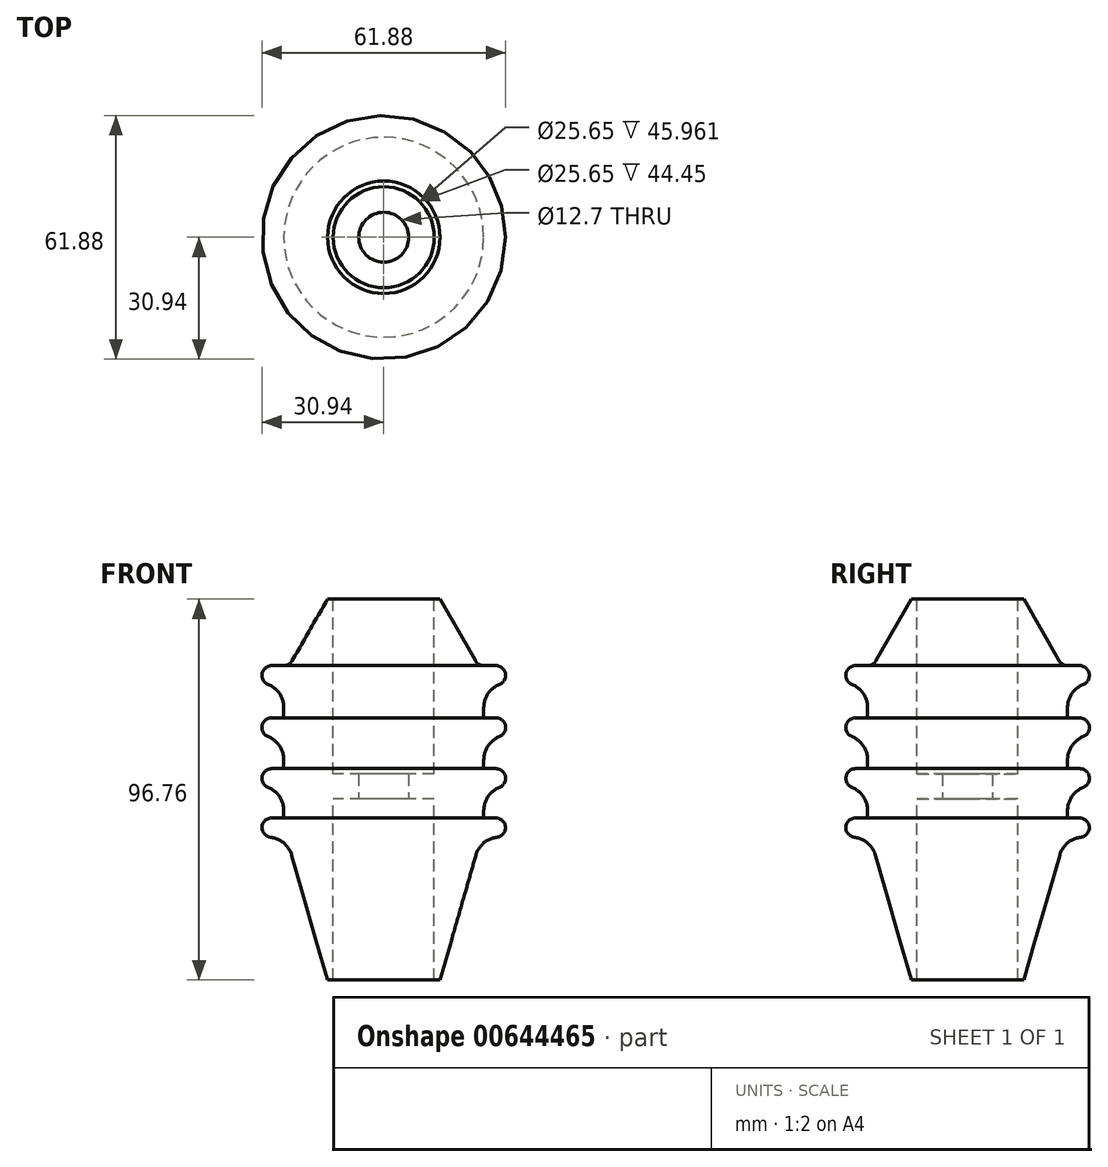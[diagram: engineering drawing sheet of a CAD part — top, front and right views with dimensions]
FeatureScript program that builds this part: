
annotation { "Feature Type Name" : "Feature", "Feature Type Description" : "" }
export const myFeature = defineFeature(function(context is Context, id is Id, definition is map)
    precondition{}
    {
        {
            var Q0;
            Q0=qCreatedBy(makeId("Front.planeOp"),FACE);
            var sketch = newSketch(context, id + "F0", { "sketchPlane" : qUnion([Q0])});
            skLineSegment(sketch, "E0", {"start": v(0, 0) * mm, "end": v(0, 96.76) * mm});
            skLineSegment(sketch, "E1", {"start": v(0, 96.76) * mm, "end": v(0, 58.06) * mm});
            skLineSegment(sketch, "E2", {"start": v(0, 0) * mm, "end": v(0, 38.7) * mm});
            skLineSegment(sketch, "E3", {"start": v(0, 96.76) * mm, "end": v(-14.29, 96.76) * mm});
            skLineSegment(sketch, "E4", {"start": v(-14.29, 96.76) * mm, "end": v(-14.29, 0) * mm});
            skLineSegment(sketch, "E5", {"start": v(-14.29, 0) * mm, "end": v(0, 0) * mm});
            skLineSegment(sketch, "E6", {"start": v(0, 96.76) * mm, "end": v(0, 77.4) * mm});
            skLineSegment(sketch, "E7", {"start": v(-25.4, 77.4) * mm, "end": v(-25.4, 38.7) * mm});
            skLineSegment(sketch, "E8", {"start": v(-25.4, 77.4) * mm, "end": v(-14.29, 96.76) * mm});
            skLineSegment(sketch, "E9", {"start": v(-25.4, 38.7) * mm, "end": v(-14.29, 0) * mm});
            skLineSegment(sketch, "E10", {"start": v(-25.4, 77.4) * mm, "end": v(-25.4, 64.14) * mm});
            skLineSegment(sketch, "E11", {"start": v(-25.4, 64.14) * mm, "end": v(-25.4, 51.24) * mm});
            skLineSegment(sketch, "E12", {"start": v(-25.4, 77.4) * mm, "end": v(-25.4, 74.95) * mm});
            skLineSegment(sketch, "E13", {"start": v(-25.4, 77.4) * mm, "end": v(-25.4, 79.87) * mm});
            skLineSegment(sketch, "E14", {"start": v(-25.4, 79.87) * mm, "end": v(0, 79.87) * mm});
            skLineSegment(sketch, "E15", {"start": v(-25.4, 64.14) * mm, "end": v(-25.4, 66.6) * mm});
            skLineSegment(sketch, "E16", {"start": v(-25.4, 64.14) * mm, "end": v(-25.4, 61.68) * mm});
            skLineSegment(sketch, "E17", {"start": v(-25.4, 61.68) * mm, "end": v(0, 61.68) * mm});
            skLineSegment(sketch, "E18", {"start": v(-25.4, 66.6) * mm, "end": v(0, 66.6) * mm});
            skLineSegment(sketch, "E19", {"start": v(-25.4, 74.95) * mm, "end": v(0, 74.95) * mm});
            skLineSegment(sketch, "E20", {"start": v(-25.4, 51.24) * mm, "end": v(-25.4, 53.7) * mm});
            skLineSegment(sketch, "E21", {"start": v(-25.4, 51.24) * mm, "end": v(-25.4, 48.77) * mm});
            skLineSegment(sketch, "E22", {"start": v(-25.4, 48.77) * mm, "end": v(0, 48.77) * mm});
            skLineSegment(sketch, "E23", {"start": v(-25.4, 53.7) * mm, "end": v(0, 53.7) * mm});
            skLineSegment(sketch, "E24", {"start": v(-25.4, 38.7) * mm, "end": v(-25.4, 41.17) * mm});
            skLineSegment(sketch, "E25", {"start": v(-25.4, 38.7) * mm, "end": v(-25.4, 36.24) * mm});
            skLineSegment(sketch, "E26", {"start": v(-25.4, 36.24) * mm, "end": v(0, 36.24) * mm});
            skLineSegment(sketch, "E27", {"start": v(-25.4, 41.17) * mm, "end": v(0, 41.17) * mm});
            skLineSegment(sketch, "E28", {"start": v(-25.4, 79.87) * mm, "end": v(-28.48, 79.87) * mm});
            skLineSegment(sketch, "E29", {"start": v(-25.4, 36.24) * mm, "end": v(-28.48, 36.24) * mm});
            skLineSegment(sketch, "E30", {"start": v(-28.48, 36.24) * mm, "end": v(-28.48, 41.17) * mm});
            skLineSegment(sketch, "E31", {"start": v(-25.4, 74.95) * mm, "end": v(-28.48, 74.95) * mm});
            skLineSegment(sketch, "E32", {"start": v(-25.4, 66.6) * mm, "end": v(-28.48, 66.6) * mm});
            skLineSegment(sketch, "E33", {"start": v(-25.4, 61.68) * mm, "end": v(-28.48, 61.68) * mm});
            skLineSegment(sketch, "E34", {"start": v(-25.4, 53.7) * mm, "end": v(-28.48, 53.7) * mm});
            skLineSegment(sketch, "E35", {"start": v(-25.4, 48.77) * mm, "end": v(-28.48, 48.77) * mm});
            skLineSegment(sketch, "E36", {"start": v(-25.4, 41.17) * mm, "end": v(-28.48, 41.17) * mm});
            skLineSegment(sketch, "E37.trimOffspring", {"start": v(-28.48, 74.95) * mm, "end": v(-28.48, 79.87) * mm});
            skLineSegment(sketch, "E38.trimOffspring", {"start": v(-28.48, 61.68) * mm, "end": v(-28.48, 66.6) * mm});
            skLineSegment(sketch, "E39.trimOffspring", {"start": v(-28.48, 48.77) * mm, "end": v(-28.48, 53.7) * mm});
            skArc(sketch, "E40", {"start": v(-28.48, 79.87) * mm, "mid": v(-30.94, 77.4) * mm, "end": v(-28.48, 74.95) * mm});
            skArc(sketch, "E41", {"start": v(-28.48, 66.6) * mm, "mid": v(-30.94, 64.14) * mm, "end": v(-28.48, 61.68) * mm});
            skArc(sketch, "E42", {"start": v(-28.48, 53.7) * mm, "mid": v(-30.94, 51.24) * mm, "end": v(-28.48, 48.77) * mm});
            skArc(sketch, "E43", {"start": v(-28.48, 41.17) * mm, "mid": v(-30.94, 38.7) * mm, "end": v(-28.48, 36.24) * mm});
            skLineSegment(sketch, "E44", {"start": v(-24.7, 36.24) * mm, "end": v(-14.29, 0) * mm});
            skLineSegment(sketch, "E45", {"start": v(-14.29, 0) * mm, "end": v(-16.02, 6.04) * mm});
            skLineSegment(sketch, "E46", {"start": v(-24.7, 36.24) * mm, "end": v(-18.26, 13.85) * mm});
            skLineSegment(sketch, "E47", {"start": v(-16.02, 6.04) * mm, "end": v(-18.26, 13.85) * mm});
            skLineSegment(sketch, "E48", {"start": v(-18.26, 13.85) * mm, "end": v(-20.5, 21.66) * mm});
            skLineSegment(sketch, "E49", {"start": v(-20.5, 21.66) * mm, "end": v(-19.76, 19.06) * mm});
            skLineSegment(sketch, "E50", {"start": v(-19.76, 19.06) * mm, "end": v(-19.01, 16.45) * mm});
            skLineSegment(sketch, "E51", {"start": v(-19.01, 16.45) * mm, "end": v(-18.26, 13.85) * mm});
            skLineSegment(sketch, "E52", {"start": v(-18.26, 13.85) * mm, "end": v(-17.52, 11.24) * mm});
            skLineSegment(sketch, "E53", {"start": v(-17.52, 11.24) * mm, "end": v(-16.77, 8.64) * mm});
            skLineSegment(sketch, "E54", {"start": v(-16.77, 8.64) * mm, "end": v(-16.02, 6.04) * mm});
            skLineSegment(sketch, "E55", {"start": v(-20.5, 21.66) * mm, "end": v(-23.05, 21.66) * mm});
            skLineSegment(sketch, "E56", {"start": v(-23.05, 21.66) * mm, "end": v(-23.05, 9.97) * mm});
            skLineSegment(sketch, "E57", {"start": v(-17.52, 11.24) * mm, "end": v(-23.05, 11.24) * mm});
            skLineSegment(sketch, "E58", {"start": v(-23.05, 11.24) * mm, "end": v(-17.52, 11.24) * mm});
            skLineSegment(sketch, "E59", {"start": v(-18.26, 13.85) * mm, "end": v(-23.05, 13.85) * mm});
            skLineSegment(sketch, "E60", {"start": v(-23.05, 13.85) * mm, "end": v(-18.26, 13.85) * mm});
            skLineSegment(sketch, "E61", {"start": v(-19.01, 16.45) * mm, "end": v(-23.05, 16.45) * mm});
            skLineSegment(sketch, "E62", {"start": v(-23.05, 16.45) * mm, "end": v(-19.01, 16.45) * mm});
            skLineSegment(sketch, "E63", {"start": v(-19.76, 19.06) * mm, "end": v(-23.05, 19.06) * mm});
            skLineSegment(sketch, "E64", {"start": v(-23.05, 19.06) * mm, "end": v(-19.76, 19.06) * mm});
            skArc(sketch, "E65", {"start": v(-23.05, 22.93) * mm, "mid": v(-24.32, 21.66) * mm, "end": v(-23.05, 20.39) * mm});
            skArc(sketch, "E66", {"start": v(-23.05, 20.33) * mm, "mid": v(-24.32, 19.06) * mm, "end": v(-23.05, 17.79) * mm});
            skArc(sketch, "E67", {"start": v(-23.05, 17.72) * mm, "mid": v(-24.32, 16.45) * mm, "end": v(-23.05, 15.18) * mm});
            skArc(sketch, "E68", {"start": v(-23.05, 15.12) * mm, "mid": v(-24.32, 13.85) * mm, "end": v(-23.05, 12.58) * mm});
            skArc(sketch, "E69", {"start": v(-23.05, 12.51) * mm, "mid": v(-24.32, 11.24) * mm, "end": v(-23.05, 9.97) * mm});
            skLineSegment(sketch, "E70", {"start": v(-23.05, 22.93) * mm, "end": v(-20.87, 22.93) * mm});
            skLineSegment(sketch, "E71", {"start": v(-23.05, 9.97) * mm, "end": v(-17.15, 9.97) * mm});
            skPoint(sketch, "E72.end.orphan", {"position": v(-23.05, 8.64) * mm});
            skPoint(sketch, "E73.start.orphan", {"position": v(-23.05, 6.04) * mm});
            skSolve(sketch);
        }
        {
            var Q0;
            Q0=qSketchRegion(id+"F0",true);
            var Q1;
            Q1=sQuery(id+"F0.wireOp",EDGE,"E6");
            revolve(context, id + "F1", {"entities" : qUnion([Q0]), "axis" : qUnion([Q1]), "revolveType" : RevolveType.FULL});
        }
        {
            var Q0;
            Q0=makeQuery(id+"F1.opRevolve","SWEPT_EDGE",EDGE,{"disambiguationData":[OSD([sQuery(id+"F0.wireOp",EDGE,"E9"),sQuery(id+"F0.wireOp",EDGE,"E26")])]});
            var Q1;
            Q1=makeQuery(id+"F1.opRevolve","SWEPT_EDGE",EDGE,{"disambiguationData":[OSD([sQuery(id+"F0.wireOp",EDGE,"E7"),sQuery(id+"F0.wireOp",EDGE,"E21"),sQuery(id+"F0.wireOp",EDGE,"E22"),sQuery(id+"F0.wireOp",EDGE,"E35")])]});
            var Q2;
            Q2=makeQuery(id+"F1.opRevolve","SWEPT_EDGE",EDGE,{"disambiguationData":[OSD([sQuery(id+"F0.wireOp",EDGE,"E11"),sQuery(id+"F0.wireOp",EDGE,"E16"),sQuery(id+"F0.wireOp",EDGE,"E17"),sQuery(id+"F0.wireOp",EDGE,"E33")])]});
            var Q3;
            Q3=makeQuery(id+"F1.opRevolve","SWEPT_EDGE",EDGE,{"disambiguationData":[OSD([sQuery(id+"F0.wireOp",EDGE,"E10"),sQuery(id+"F0.wireOp",EDGE,"E12"),sQuery(id+"F0.wireOp",EDGE,"E19"),sQuery(id+"F0.wireOp",EDGE,"E31")])]});
            fillet(context, id + "F2", {"entities" : qUnion([Q0, Q1, Q2, Q3]), "radius" : 6.35 * mm, "tangentPropagation" : true, "allowEdgeOverflow" : false});
        }
        {
            var Q0;
            Q0=makeQuery(id+"F1.opRevolve","SWEPT_EDGE",EDGE,{"disambiguationData":[OSD([sQuery(id+"F0.wireOp",EDGE,"E8"),sQuery(id+"F0.wireOp",EDGE,"E14")])]});
            fillet(context, id + "F3", {"entities" : qUnion([Q0]), "radius" : 2.54 * mm, "tangentPropagation" : true, "allowEdgeOverflow" : false});
        }
        {
            var Q0;
            Q0=makeQuery(id+"F1.opRevolve","SWEPT_FACE",FACE,{"disambiguationData":[OSD([sQuery(id+"F0.wireOp",EDGE,"E3")])]});
            var sketch = newSketch(context, id + "F4", { "sketchPlane" : qUnion([Q0])});
            skCircle(sketch, "E74", {"center": v(0, 0) * mm, "radius": 12.83 * mm});
            skSolve(sketch);
        }
        {
            var Q0;
            Q0=qSketchRegion(id+"F4",true);
            extrude(context, id + "F5", {"entities" : qUnion([Q0]), "operationType" : NewBodyOperationType.REMOVE, "endBound" : BoundingType.THROUGH_ALL, "oppositeDirection" : true, "depth" : 25.4 * mm, "offsetDistance" : 25.4 * mm});
        }
        {
            var Q0;
            Q0=makeQuery(id+"F1.opRevolve","SWEPT_FACE",FACE,{"disambiguationData":[OSD([sQuery(id+"F0.wireOp",EDGE,"E3")])]});
            cPlane(context, id + "F6", {"entities" : qUnion([Q0]), "cplaneType" : CPlaneType.OFFSET, "offset" : 50.8 * mm, "oppositeDirection" : true, "width" : 152.4 * mm, "height" : 152.4 * mm});
        }
        {
            var Q0;
            Q0=qCreatedBy(id+"F6.planeOp",FACE);
            var sketch = newSketch(context, id + "F7", { "sketchPlane" : qUnion([Q0])});
            skCircle(sketch, "E75", {"center": v(0, 0) * mm, "radius": 14.29 * mm});
            skCircle(sketch, "E76", {"center": v(0, 0) * mm, "radius": 6.35 * mm});
            skSolve(sketch);
        }
        {
            var Q0;
            Q0 = qSketchRegion(id + "F7", true);
            extrude(context, id + "F8", {"entities" : qUnion([Q0]), "operationType" : NewBodyOperationType.ADD, "depth" : 6.35 * mm, "offsetDistance" : 25.4 * mm});
        }
        {
            var Q0;
            Q0=qCreatedBy(makeId("Front.planeOp"),FACE);
            var sketch = newSketch(context, id + "F9", { "sketchPlane" : qUnion([Q0])});
            skLineSegment(sketch, "E77", {"start": v(-23.4, 31.7) * mm, "end": v(-14.29, 0) * mm});
            skLineSegment(sketch, "E78", {"start": v(-23.4, 31.7) * mm, "end": v(-28.54, 31.7) * mm});
            skLineSegment(sketch, "E79", {"start": v(-28.54, 31.7) * mm, "end": v(-28.54, 0) * mm});
            skLineSegment(sketch, "E80", {"start": v(-28.54, 0) * mm, "end": v(-14.29, 0) * mm});
            skLineSegment(sketch, "E81", {"start": v(0, 0) * mm, "end": v(0, 9.34) * mm});
            skSolve(sketch);
        }
        {
            var Q0;
            Q0 = qSketchRegion(id + "F9", true);
            var Q1;
            Q1=sQuery(id+"F9.wireOp",EDGE,"E81");
            revolve(context, id + "F10", {"operationType" : NewBodyOperationType.REMOVE, "surfaceOperationType" : NewSurfaceOperationType.NEW, "entities" : qUnion([Q0]), "axis" : qUnion([Q1]), "revolveType" : RevolveType.FULL, "oppositeDirection" : true});
        }
    });
